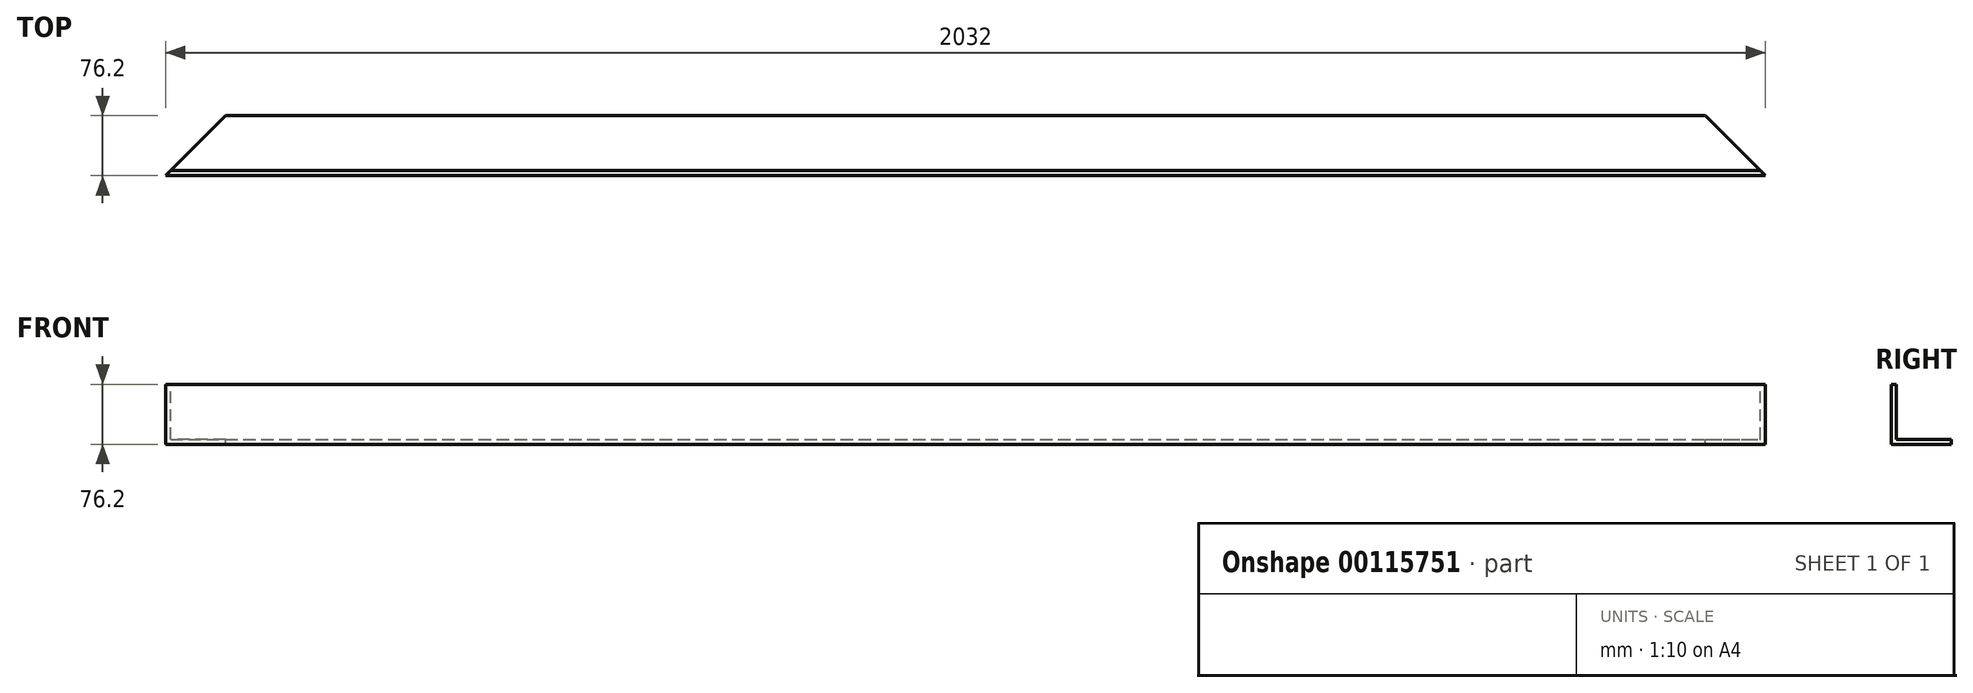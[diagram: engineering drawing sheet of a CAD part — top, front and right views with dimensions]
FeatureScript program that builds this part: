
annotation { "Feature Type Name" : "Feature", "Feature Type Description" : "" }
export const myFeature = defineFeature(function(context is Context, id is Id, definition is map)
    precondition{}
    {
        {
            var Q0;
            Q0=qCreatedBy(makeId("Right.planeOp"),FACE);
            var sketch = newSketch(context, id + "F0", { "sketchPlane" : qUnion([Q0])});
            skLineSegment(sketch, "E0", {"start": v(0, 76.2) * mm, "end": v(0, 0) * mm});
            skLineSegment(sketch, "E1", {"start": v(0, 0) * mm, "end": v(76.2, 0) * mm});
            skLineSegment(sketch, "E2.0", {"start": v(6.35, 6.35) * mm, "end": v(76.2, 6.35) * mm});
            skLineSegment(sketch, "E2.1", {"start": v(6.35, 76.2) * mm, "end": v(6.35, 6.35) * mm});
            skLineSegment(sketch, "E3", {"start": v(0, 76.2) * mm, "end": v(6.35, 76.2) * mm});
            skLineSegment(sketch, "E4", {"start": v(76.2, 6.35) * mm, "end": v(76.2, 0) * mm});
            skSolve(sketch);
        }
        {
            var Q0;
            Q0 = qSketchRegion(id + "F0", true);
            extrude(context, id + "F1", {"entities" : qUnion([Q0]), "oppositeDirection" : true, "depth" : 2032 * mm});
        }
        {
            var Q0;
            Q0=makeQuery(id+"F1.opExtrude","SWEPT_FACE",FACE,{"disambiguationData":[OSD([sQuery(id+"F0.wireOp",EDGE,"E3")])]});
            var sketch = newSketch(context, id + "F2", { "sketchPlane" : qUnion([Q0])});
            skLineSegment(sketch, "E5", {"start": v(0, 76.2) * mm, "end": v(0, 0) * mm});
            skLineSegment(sketch, "E6", {"start": v(0, 0) * mm, "end": v(-76.2, 76.2) * mm});
            skLineSegment(sketch, "E7.trimOffspring", {"start": v(-76.2, 76.2) * mm, "end": v(0, 76.2) * mm});
            skLineSegment(sketch, "E8", {"start": v(-2032, 0) * mm, "end": v(-1955.8, 76.2) * mm});
            skLineSegment(sketch, "E9", {"start": v(-2032, 0) * mm, "end": v(-2032, 76.2) * mm});
            skLineSegment(sketch, "E10", {"start": v(-2032, 76.2) * mm, "end": v(-1955.8, 76.2) * mm});
            skSolve(sketch);
        }
        {
            var Q0;
            Q0 = qSketchRegion(id + "F2", true);
            extrude(context, id + "F3", {"entities" : qUnion([Q0]), "operationType" : NewBodyOperationType.REMOVE, "oppositeDirection" : true, "depth" : 76.2 * mm});
        }
    });
